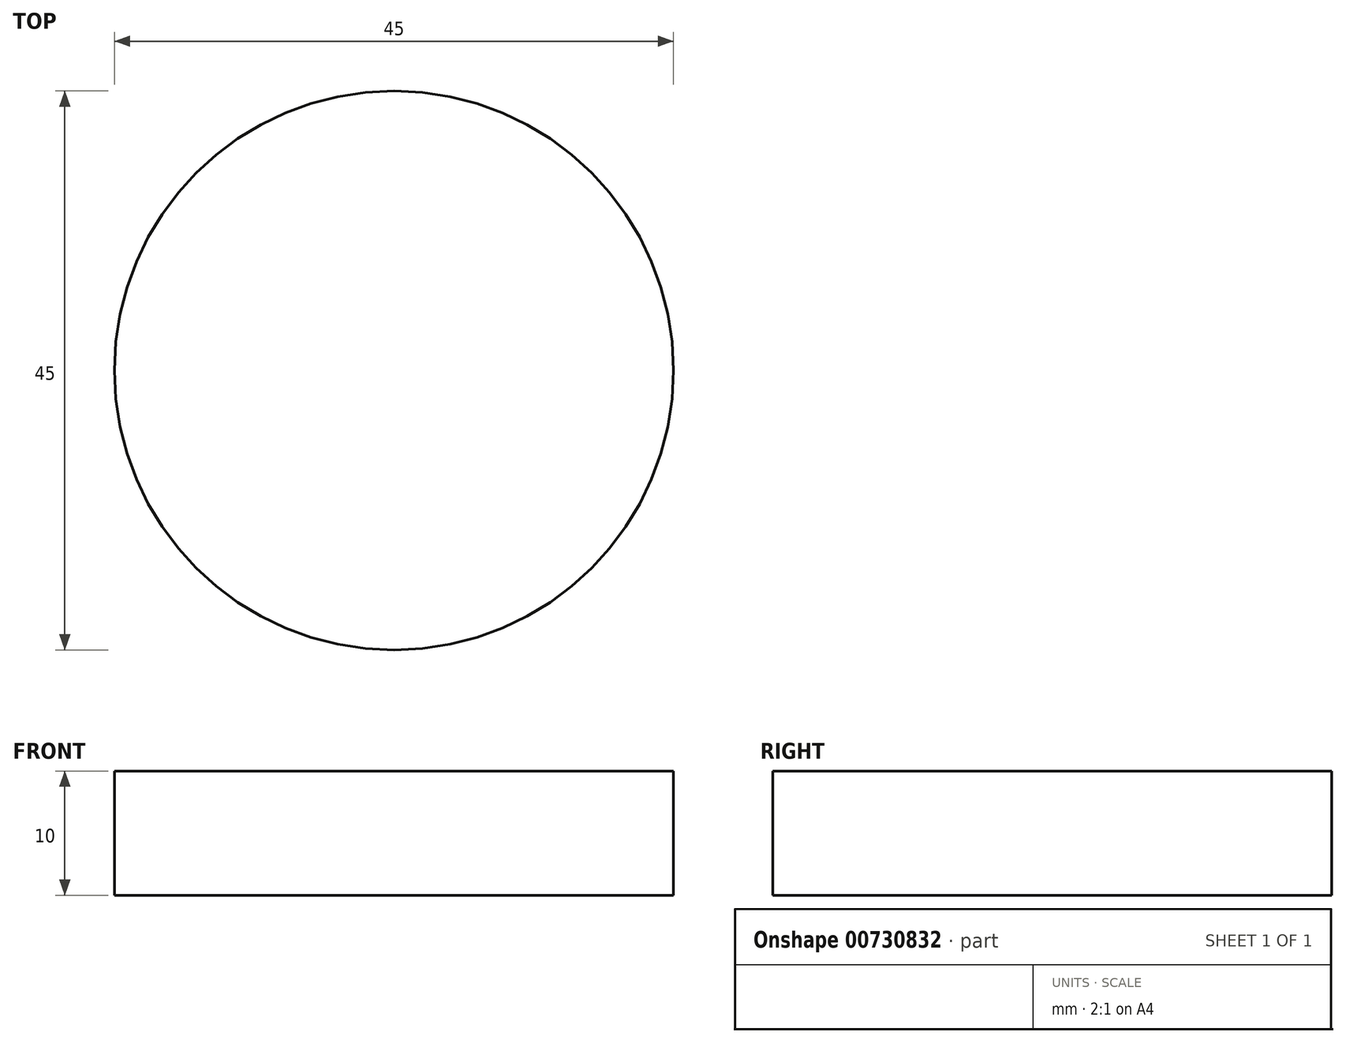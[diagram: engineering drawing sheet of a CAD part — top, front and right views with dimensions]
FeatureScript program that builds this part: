
annotation { "Feature Type Name" : "Feature", "Feature Type Description" : "" }
export const myFeature = defineFeature(function(context is Context, id is Id, definition is map)
    precondition{}
    {
        {
            var Q0;
            Q0=qCreatedBy(makeId("Top.planeOp"),FACE);
            var sketch = newSketch(context, id + "F0", { "sketchPlane" : qUnion([Q0])});
            skCircle(sketch, "E0", {"center": v(0, 0) * mm, "radius": 22.5 * mm});
            skSolve(sketch);
        }
        {
            var Q0;
            Q0 = qSketchRegion(id + "F0", true);
            extrude(context, id + "F1", {"entities" : qUnion([Q0]), "depth" : 10 * mm, "offsetDistance" : 25.4 * mm});
        }
    });
